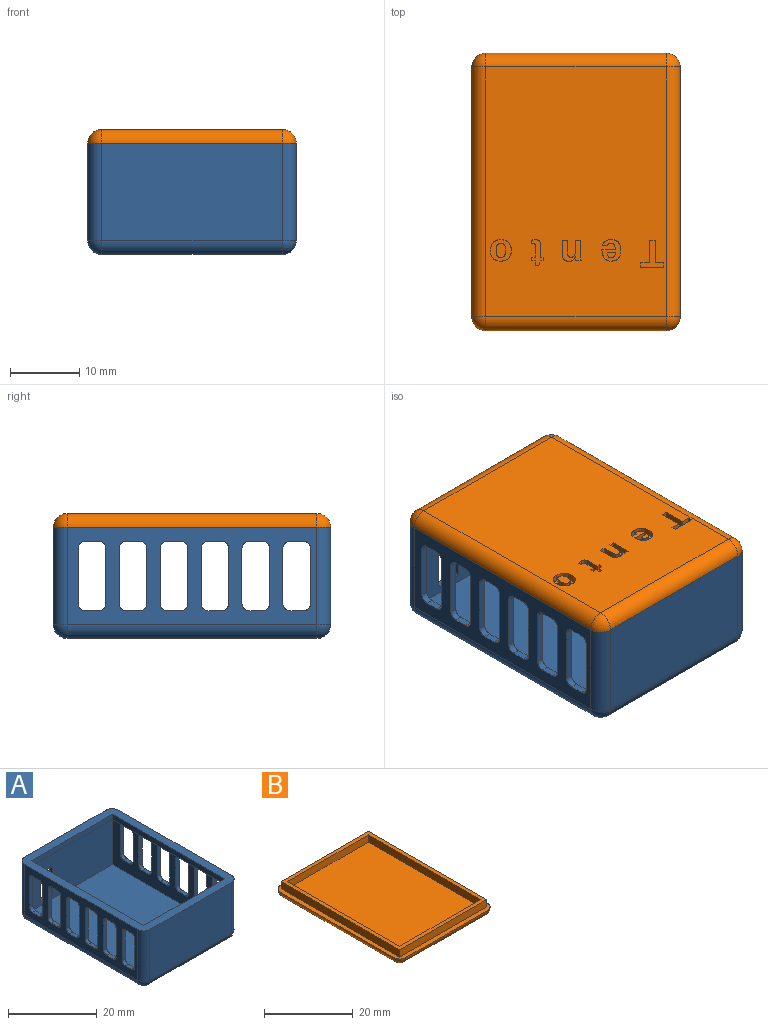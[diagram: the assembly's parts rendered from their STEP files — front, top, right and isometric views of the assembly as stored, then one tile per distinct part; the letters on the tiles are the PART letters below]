
ASSEMBLY  parts=2 mates=1
PART A: 125 faces, bbox 30x40x16 mm
  f0: plane 27.8x0.5mm, normal (0,-1,0), area 13.9mm2, adj f58,f109,f110,f116
  f1: plane 28x13mm, normal (0,-1,0), area 332.2mm2, adj f2,f4,f10,f16,f17,f18,f19,f20
  f2: plane 38x13mm, normal (-1,0,0), area 259.2mm2, adj f1,f3,f10,f42,f43,f44,f45,f46
  f3: plane 28x13mm, normal (0,1,0), area 364mm2, adj f2,f4,f10,f58
  f4: plane 38x13mm, normal (1,0,0), area 259.2mm2, adj f1,f3,f10,f24,f25,f26,f27,f28
  f5: plane 36x14mm, normal (1,0,0), area 269.2mm2, adj f9,f15,f42,f43,f44,f45,f46,f47
  f6: plane 26x14mm, normal (0,1,0), area 332.2mm2, adj f9,f14,f16,f17,f18,f20,f21,f22
  f7: plane 36x14mm, normal (-1,0,0), area 269.2mm2, adj f9,f12,f24,f25,f26,f27,f28,f29
  f8: plane 26x14mm, normal (0,-1,0), area 364mm2, adj f9,f13,f121,f123
  f9: plane 40x30mm, normal (0,0,1), area 272.9mm2, adj f5,f6,f7,f8,f112,f113,f114,f115
  f10: plane 38x28mm, normal (0,0,1), area 1064mm2, adj f1,f2,f3,f4
  f11: plane 36x26mm, normal (0,0,-1), area 936mm2, adj f12,f13,f14,f15
  f12: cylinder r=2mm len=36mm, axis (0,-1,0), area 113.1mm2, adj f7,f11,f120,f122
  f13: cylinder r=2mm len=26mm, axis (-1,0,0), area 81.7mm2, adj f8,f11,f122,f124
  f14: cylinder r=2mm len=26mm, axis (-1,0,0), area 81.7mm2, adj f6,f11,f19,f118,f120
  f15: cylinder r=2mm len=36mm, axis (0,-1,0), area 113.1mm2, adj f5,f11,f118,f124
  f16: plane 7x1mm, normal (1,0,0), area 7mm2, adj f1,f6,f20,f23
  f17: plane 3x1mm, normal (0,0,-1), area 3mm2, adj f1,f6,f20,f21
  f18: plane 7x1mm, normal (-1,0,0), area 7mm2, adj f1,f6,f21,f22
  f19: plane 3x1mm, normal (0,0,1), area 3mm2, adj f1,f14,f22,f23
  f20: cylinder r=0.5mm len=1mm, axis (0,-1,0), area 0.8mm2, adj f1,f6,f16,f17
  f21: cylinder r=0.5mm len=1mm, axis (0,-1,0), area 0.8mm2, adj f1,f6,f17,f18
  f22: cylinder r=0.5mm len=1mm, axis (0,1,0), area 0.8mm2, adj f1,f6,f18,f19
  f23: cylinder r=0.5mm len=1mm, axis (0,1,0), area 0.8mm2, adj f1,f6,f16,f19
  f24: plane 2x1mm, normal (0,0,1), area 2mm2, adj f4,f7,f105,f106
  f25: plane 8x1mm, normal (0,1,0), area 8mm2, adj f4,f7,f106,f107
  f26: plane 8x1mm, normal (0,-1,0), area 8mm2, adj f4,f7,f105,f108
  f27: plane 2x1mm, normal (0,0,1), area 2mm2, adj f4,f7,f103,f104
  f28: plane 8x1mm, normal (0,1,0), area 8mm2, adj f4,f7,f102,f103
  f29: plane 8x1mm, normal (0,-1,0), area 8mm2, adj f4,f7,f101,f104
  f30: plane 2x1mm, normal (0,0,1), area 2mm2, adj f4,f7,f97,f98
  f31: plane 8x1mm, normal (0,1,0), area 8mm2, adj f4,f7,f98,f99
  f32: plane 8x1mm, normal (0,-1,0), area 8mm2, adj f4,f7,f97,f100
  f33: plane 2x1mm, normal (0,0,1), area 2mm2, adj f4,f7,f93,f94
  f34: plane 8x1mm, normal (0,1,0), area 8mm2, adj f4,f7,f94,f95
  f35: plane 8x1mm, normal (0,-1,0), area 8mm2, adj f4,f7,f93,f96
  f36: plane 2x1mm, normal (0,0,1), area 2mm2, adj f4,f7,f89,f90
  f37: plane 8x1mm, normal (0,1,0), area 8mm2, adj f4,f7,f90,f91
  f38: plane 8x1mm, normal (0,-1,0), area 8mm2, adj f4,f7,f89,f92
  f39: plane 2x1mm, normal (0,0,1), area 2mm2, adj f4,f7,f85,f86
  f40: plane 8x1mm, normal (0,1,0), area 8mm2, adj f4,f7,f86,f87
  f41: plane 8x1mm, normal (0,-1,0), area 8mm2, adj f4,f7,f85,f88
  f42: plane 8x1mm, normal (0,-1,0), area 8mm2, adj f2,f5,f81,f83
  f43: plane 8x1mm, normal (0,1,0), area 8mm2, adj f2,f5,f82,f84
  f44: plane 2x1mm, normal (0,0,1), area 2mm2, adj f2,f5,f83,f84
  f45: plane 8x1mm, normal (0,-1,0), area 8mm2, adj f2,f5,f77,f79
  f46: plane 8x1mm, normal (0,1,0), area 8mm2, adj f2,f5,f78,f80
  f47: plane 2x1mm, normal (0,0,1), area 2mm2, adj f2,f5,f79,f80
  f48: plane 8x1mm, normal (0,-1,0), area 8mm2, adj f2,f5,f73,f75
  f49: plane 8x1mm, normal (0,1,0), area 8mm2, adj f2,f5,f74,f76
  f50: plane 2x1mm, normal (0,0,1), area 2mm2, adj f2,f5,f75,f76
  f51: plane 8x1mm, normal (0,-1,0), area 8mm2, adj f2,f5,f69,f71
  f52: plane 8x1mm, normal (0,1,0), area 8mm2, adj f2,f5,f70,f72
  f53: plane 2x1mm, normal (0,0,1), area 2mm2, adj f2,f5,f71,f72
  f54: plane 8x1mm, normal (0,-1,0), area 8mm2, adj f2,f5,f65,f67
  f55: plane 8x1mm, normal (0,1,0), area 8mm2, adj f2,f5,f66,f68
  f56: plane 2x1mm, normal (0,0,1), area 2mm2, adj f2,f5,f67,f68
  f57: plane 8x1mm, normal (0,-1,0), area 8mm2, adj f2,f5,f61,f63
  f58: plane 38x30mm, normal (0,0,-1), area 37.2mm2, adj f0,f1,f2,f3,f4,f5,f7,f61
  f59: plane 8x1mm, normal (0,1,0), area 8mm2, adj f2,f5,f62,f64
  f60: plane 2x1mm, normal (0,0,1), area 2mm2, adj f2,f5,f63,f64
  f61: cylinder r=1mm len=1mm, axis (-1,0,0), area 1.6mm2, adj f2,f5,f57,f58
  f62: cylinder r=1mm len=1mm, axis (1,0,0), area 1.6mm2, adj f2,f5,f58,f59
  f63: cylinder r=1mm len=1mm, axis (1,0,0), area 1.6mm2, adj f2,f5,f57,f60
  f64: cylinder r=1mm len=1mm, axis (-1,0,0), area 1.6mm2, adj f2,f5,f59,f60
  f65: cylinder r=1mm len=1mm, axis (-1,0,0), area 1.6mm2, adj f2,f5,f54,f58
  f66: cylinder r=1mm len=1mm, axis (1,0,0), area 1.6mm2, adj f2,f5,f55,f58
  f67: cylinder r=1mm len=1mm, axis (1,0,0), area 1.6mm2, adj f2,f5,f54,f56
  f68: cylinder r=1mm len=1mm, axis (-1,0,0), area 1.6mm2, adj f2,f5,f55,f56
  f69: cylinder r=1mm len=1mm, axis (-1,0,0), area 1.6mm2, adj f2,f5,f51,f58
  f70: cylinder r=1mm len=1mm, axis (1,0,0), area 1.6mm2, adj f2,f5,f52,f58
  f71: cylinder r=1mm len=1mm, axis (1,0,0), area 1.6mm2, adj f2,f5,f51,f53
  f72: cylinder r=1mm len=1mm, axis (-1,0,0), area 1.6mm2, adj f2,f5,f52,f53
  f73: cylinder r=1mm len=1mm, axis (-1,0,0), area 1.6mm2, adj f2,f5,f48,f58
  f74: cylinder r=1mm len=1mm, axis (1,0,0), area 1.6mm2, adj f2,f5,f49,f58
  f75: cylinder r=1mm len=1mm, axis (1,0,0), area 1.6mm2, adj f2,f5,f48,f50
  f76: cylinder r=1mm len=1mm, axis (-1,0,0), area 1.6mm2, adj f2,f5,f49,f50
  f77: cylinder r=1mm len=1mm, axis (-1,0,0), area 1.6mm2, adj f2,f5,f45,f58
  f78: cylinder r=1mm len=1mm, axis (1,0,0), area 1.6mm2, adj f2,f5,f46,f58
  f79: cylinder r=1mm len=1mm, axis (1,0,0), area 1.6mm2, adj f2,f5,f45,f47
  f80: cylinder r=1mm len=1mm, axis (-1,0,0), area 1.6mm2, adj f2,f5,f46,f47
  f81: cylinder r=1mm len=1mm, axis (-1,0,0), area 1.6mm2, adj f2,f5,f42,f58
  f82: cylinder r=1mm len=1mm, axis (1,0,0), area 1.6mm2, adj f2,f5,f43,f58
  f83: cylinder r=1mm len=1mm, axis (1,0,0), area 1.6mm2, adj f2,f5,f42,f44
  f84: cylinder r=1mm len=1mm, axis (-1,0,0), area 1.6mm2, adj f2,f5,f43,f44
  f85: cylinder r=1mm len=1mm, axis (1,0,0), area 1.6mm2, adj f4,f7,f39,f41
  f86: cylinder r=1mm len=1mm, axis (-1,0,0), area 1.6mm2, adj f4,f7,f39,f40
  f87: cylinder r=1mm len=1mm, axis (1,0,0), area 1.6mm2, adj f4,f7,f40,f58
  f88: cylinder r=1mm len=1mm, axis (-1,0,0), area 1.6mm2, adj f4,f7,f41,f58
  f89: cylinder r=1mm len=1mm, axis (1,0,0), area 1.6mm2, adj f4,f7,f36,f38
  f90: cylinder r=1mm len=1mm, axis (-1,0,0), area 1.6mm2, adj f4,f7,f36,f37
  f91: cylinder r=1mm len=1mm, axis (1,0,0), area 1.6mm2, adj f4,f7,f37,f58
  f92: cylinder r=1mm len=1mm, axis (-1,0,0), area 1.6mm2, adj f4,f7,f38,f58
  f93: cylinder r=1mm len=1mm, axis (1,0,0), area 1.6mm2, adj f4,f7,f33,f35
  f94: cylinder r=1mm len=1mm, axis (-1,0,0), area 1.6mm2, adj f4,f7,f33,f34
  f95: cylinder r=1mm len=1mm, axis (1,0,0), area 1.6mm2, adj f4,f7,f34,f58
  f96: cylinder r=1mm len=1mm, axis (-1,0,0), area 1.6mm2, adj f4,f7,f35,f58
  f97: cylinder r=1mm len=1mm, axis (1,0,0), area 1.6mm2, adj f4,f7,f30,f32
  f98: cylinder r=1mm len=1mm, axis (-1,0,0), area 1.6mm2, adj f4,f7,f30,f31
  f99: cylinder r=1mm len=1mm, axis (1,0,0), area 1.6mm2, adj f4,f7,f31,f58
  f100: cylinder r=1mm len=1mm, axis (-1,0,0), area 1.6mm2, adj f4,f7,f32,f58
  f101: cylinder r=1mm len=1mm, axis (-1,0,0), area 1.6mm2, adj f4,f7,f29,f58
  f102: cylinder r=1mm len=1mm, axis (1,0,0), area 1.6mm2, adj f4,f7,f28,f58
  f103: cylinder r=1mm len=1mm, axis (-1,0,0), area 1.6mm2, adj f4,f7,f27,f28
  f104: cylinder r=1mm len=1mm, axis (1,0,0), area 1.6mm2, adj f4,f7,f27,f29
  f105: cylinder r=1mm len=1mm, axis (1,0,0), area 1.6mm2, adj f4,f7,f24,f26
  f106: cylinder r=1mm len=1mm, axis (-1,0,0), area 1.6mm2, adj f4,f7,f24,f25
  f107: cylinder r=1mm len=1mm, axis (1,0,0), area 1.6mm2, adj f4,f7,f25,f58
  f108: cylinder r=1mm len=1mm, axis (-1,0,0), area 1.6mm2, adj f4,f7,f26,f58
  f109: plane 37.8x0.5mm, normal (1,0,0), area 18.9mm2, adj f0,f58,f111,f116
  f110: plane 37.8x0.5mm, normal (-1,0,0), area 18.9mm2, adj f0,f58,f111,f116
  f111: plane 27.8x0.5mm, normal (0,1,0), area 13.9mm2, adj f58,f109,f110,f116
  f112: plane 25.8x1.5mm, normal (0,-1,0), area 38.7mm2, adj f9,f113,f115,f116
  f113: plane 35.8x1.5mm, normal (-1,0,0), area 53.7mm2, adj f9,f112,f114,f116
  f114: plane 25.8x1.5mm, normal (0,1,0), area 38.7mm2, adj f9,f113,f115,f116
  f115: plane 35.8x1.5mm, normal (1,0,0), area 53.7mm2, adj f9,f112,f114,f116
  f116: plane 37.8x27.8mm, normal (0,0,-1), area 127.2mm2, adj f0,f109,f110,f111,f112,f113,f114,f115
  f117: cylinder r=2mm len=14mm, axis (0,0,1), area 44mm2, adj f5,f6,f9,f118
  f118: sphere r=2mm, area 6.3mm2, adj f14,f15,f117
  f119: cylinder r=2mm len=14mm, axis (0,0,-1), area 44mm2, adj f6,f7,f9,f120
  f120: sphere r=2mm, area 6.3mm2, adj f12,f14,f119
  f121: cylinder r=2mm len=14mm, axis (0,0,1), area 44mm2, adj f7,f8,f9,f122
  f122: sphere r=2mm, area 6.3mm2, adj f12,f13,f121
  f123: cylinder r=2mm len=14mm, axis (0,0,-1), area 44mm2, adj f5,f8,f9,f124
  f124: sphere r=2mm, area 6.3mm2, adj f13,f15,f123
PART B: 104 faces, bbox 30x40x4 mm
  f0: plane 36x26mm, normal (0,0,-1), area 909.2mm2, adj f13,f14,f17,f18,f25,f26,f27,f28
  f1: plane 35.8x2mm, normal (-1,0,0), area 71.6mm2, adj f2,f8,f9,f10
  f2: plane 25.8x2mm, normal (0,1,0), area 51.6mm2, adj f1,f3,f9,f10
  f3: plane 35.8x2mm, normal (1,0,0), area 71.6mm2, adj f2,f8,f9,f10
  f4: plane 37.8x2mm, normal (-1,0,0), area 75.6mm2, adj f5,f7,f9,f11
  f5: plane 27.8x2mm, normal (0,-1,0), area 55.6mm2, adj f4,f6,f9,f11
  f6: plane 37.8x2mm, normal (1,0,0), area 75.6mm2, adj f5,f7,f9,f11
  f7: plane 27.8x2mm, normal (0,1,0), area 55.6mm2, adj f4,f6,f9,f11
  f8: plane 25.8x2mm, normal (0,-1,0), area 51.6mm2, adj f1,f3,f9,f10
  f9: plane 37.8x27.8mm, normal (0,0,1), area 127.2mm2, adj f1,f2,f3,f4,f5,f6,f7,f8
  f10: plane 35.8x25.8mm, normal (0,0,1), area 923.6mm2, adj f1,f2,f3,f8
  f11: plane 40x30mm, normal (0,0,1), area 145.7mm2, adj f4,f5,f6,f7,f12,f13,f14,f15
  f12: sphere r=2mm, area 6.3mm2, adj f11,f13,f14
  f13: cylinder r=2mm len=26mm, axis (1,0,0), area 81.7mm2, adj f0,f11,f12,f15
  f14: cylinder r=2mm len=36mm, axis (0,1,0), area 113.1mm2, adj f0,f11,f12,f16
  f15: sphere r=2mm, area 6.3mm2, adj f11,f13,f17
  f16: sphere r=2mm, area 6.3mm2, adj f11,f14,f18
  f17: cylinder r=2mm len=36mm, axis (0,-1,0), area 113.1mm2, adj f0,f11,f15,f19
  f18: cylinder r=2mm len=26mm, axis (-1,0,0), area 81.7mm2, adj f0,f11,f16,f19
  f19: sphere r=2mm, area 6.3mm2, adj f11,f17,f18
  f20: extruded ~0.9x0.77mm, area 0.7mm2, adj f21,f33,f34,f102
  f21: extruded ~1.02x0.9mm, area 1.3mm2, adj f20,f22,f34,f102
  f22: extruded ~0.9x0.5mm, area 0.5mm2, adj f21,f23,f34,f102
  f23: extruded ~0.9x0.76mm, area 0.7mm2, adj f22,f24,f34,f102
  f24: extruded ~1.02x0.9mm, area 1.3mm2, adj f23,f33,f34,f102
  f25: extruded ~1.14x0.9mm, area 1.1mm2, adj f0,f26,f32,f34
  f26: extruded ~1.15x0.9mm, area 1.1mm2, adj f0,f25,f27,f34
  f27: extruded ~1.12x0.9mm, area 1.1mm2, adj f0,f26,f28,f34
  f28: extruded ~1.11x0.9mm, area 1.1mm2, adj f0,f27,f29,f34
  f29: extruded ~1.14x0.9mm, area 1.1mm2, adj f0,f28,f30,f34
  f30: extruded ~1.14x0.9mm, area 1.1mm2, adj f0,f29,f31,f34
  f31: extruded ~1.1x0.9mm, area 1.1mm2, adj f0,f30,f32,f34
  f32: extruded ~1.12x0.9mm, area 1.1mm2, adj f0,f25,f31,f34
  f33: extruded ~0.9x0.51mm, area 0.5mm2, adj f20,f24,f34,f102
  f34: plane 3.1x3.02mm, normal (0,0,-1), area 5.3mm2, adj f20,f21,f22,f23,f24,f25,f26,f27
  f35: extruded ~0.9x0.53mm, area 0.5mm2, adj f0,f36,f52,f53
  f36: extruded ~0.9x0.66mm, area 0.6mm2, adj f0,f35,f37,f53
  f37: plane 0.9x0.48mm, normal (-1,0,0), area 0.4mm2, adj f0,f36,f38,f53
  f38: extruded ~0.9x0.26mm, area 0.2mm2, adj f0,f37,f39,f53
  f39: extruded ~0.9x0.26mm, area 0.3mm2, adj f0,f38,f40,f53
  f40: extruded ~0.9x0.32mm, area 0.3mm2, adj f0,f39,f41,f53
  f41: plane 1.56x0.9mm, normal (-1,0,0), area 1.4mm2, adj f0,f40,f42,f53
  f42: plane 0.9x0.57mm, normal (0,-1,0), area 0.5mm2, adj f0,f41,f43,f53
  f43: plane 0.9x0.52mm, normal (-1,0,0), area 0.5mm2, adj f0,f42,f44,f53
  f44: plane 0.9x0.57mm, normal (0,1,0), area 0.5mm2, adj f0,f43,f45,f53
  f45: plane 0.9x0.7mm, normal (-1,0,0), area 0.6mm2, adj f0,f44,f46,f53
  f46: plane 0.9x0.49mm, normal (0,1,0), area 0.4mm2, adj f0,f45,f47,f53
  f47: plane 0.9x0.7mm, normal (0.94,0.33,0), area 0.7mm2, adj f0,f46,f48,f53
  f48: plane 0.9x0.42mm, normal (0,1,0), area 0.4mm2, adj f0,f47,f49,f53
  f49: plane 0.9x0.52mm, normal (1,0,0), area 0.5mm2, adj f0,f48,f50,f53
  f50: plane 0.9x0.38mm, normal (0,-1,0), area 0.3mm2, adj f0,f49,f51,f53
  f51: plane 1.76x0.9mm, normal (1,0,0), area 1.6mm2, adj f0,f50,f52,f53
  f52: extruded ~0.9x0.57mm, area 0.5mm2, adj f0,f35,f51,f53
  f53: plane 3.74x1.75mm, normal (0,0,-1), area 3.5mm2, adj f35,f36,f37,f38,f39,f40,f41,f42
  f54: plane 1.68x0.9mm, normal (1,0,0), area 1.5mm2, adj f0,f55,f72,f73
  f55: plane 0.9x0.77mm, normal (0,-1,0), area 0.7mm2, adj f0,f54,f56,f73
  f56: plane 1.9x0.9mm, normal (-1,0,0), area 1.7mm2, adj f0,f55,f57,f73
  f57: extruded ~0.9x0.86mm, area 0.8mm2, adj f0,f56,f58,f73
  f58: extruded ~0.9x0.73mm, area 0.7mm2, adj f0,f57,f59,f73
  f59: extruded ~0.9x0.57mm, area 0.5mm2, adj f0,f58,f60,f73
  f60: extruded ~0.9x0.5mm, area 0.6mm2, adj f0,f59,f61,f73
  f61: plane 0.9x0.01mm, normal (0,1,0), area 0mm2, adj f0,f60,f62,f73
  f62: extruded ~0.9x0.31mm, area 0.3mm2, adj f0,f61,f63,f73
  f63: extruded ~0.9x0.28mm, area 0.3mm2, adj f0,f62,f64,f73
  f64: plane 0.9x0.74mm, normal (0,1,0), area 0.7mm2, adj f0,f63,f65,f73
  f65: extruded ~0.9x0.27mm, area 0.2mm2, adj f0,f64,f66,f73
  f66: extruded ~0.9x0.39mm, area 0.4mm2, adj f0,f65,f67,f73
  f67: plane 2.32x0.9mm, normal (1,0,0), area 2.1mm2, adj f0,f66,f68,f73
  f68: plane 0.9x0.78mm, normal (0,-1,0), area 0.7mm2, adj f0,f67,f69,f73
  f69: plane 1.6x0.9mm, normal (-1,0,0), area 1.4mm2, adj f0,f68,f70,f73
  f70: extruded ~0.9x0.62mm, area 0.6mm2, adj f0,f69,f71,f73
  f71: extruded ~0.9x0.45mm, area 0.5mm2, adj f0,f70,f72,f73
  f72: extruded ~0.9x0.79mm, area 1mm2, adj f0,f54,f71,f73
  f73: plane 3.05x2.74mm, normal (0,0,-1), area 5.2mm2, adj f54,f55,f56,f57,f58,f59,f60,f61
  f74: extruded ~0.9x0.42mm, area 0.4mm2, adj f75,f91,f92,f103
  f75: extruded ~0.9x0.41mm, area 0.4mm2, adj f74,f76,f92,f103
  f76: extruded ~0.9x0.54mm, area 0.5mm2, adj f75,f77,f92,f103
  f77: plane 1.16x0.9mm, normal (0,1,0), area 1mm2, adj f76,f91,f92,f103
  f78: extruded ~1.04x0.9mm, area 1mm2, adj f0,f79,f90,f92
  f79: extruded ~1.29x0.9mm, area 1.5mm2, adj f0,f78,f80,f92
  f80: plane 0.9x0.73mm, normal (-0.09,1,0), area 0.7mm2, adj f0,f79,f81,f92
  f81: extruded ~0.9x0.52mm, area 0.6mm2, adj f0,f80,f82,f92
  f82: extruded ~0.9x0.46mm, area 0.5mm2, adj f0,f81,f83,f92
  f83: extruded ~0.9x0.66mm, area 0.6mm2, adj f0,f82,f84,f92
  f84: plane 1.92x0.9mm, normal (0,-1,0), area 1.7mm2, adj f0,f83,f85,f92
  f85: plane 0.9x0.02mm, normal (-1,0,0), area 0mm2, adj f0,f84,f86,f92
  f86: extruded ~1.25x0.9mm, area 1.2mm2, adj f0,f85,f87,f92
  f87: extruded ~0.98x0.9mm, area 1mm2, adj f0,f86,f88,f92
  f88: extruded ~1.04x0.9mm, area 1mm2, adj f0,f87,f89,f92
  f89: extruded ~1.14x0.9mm, area 1.1mm2, adj f0,f88,f90,f92
  f90: extruded ~1.17x0.9mm, area 1.1mm2, adj f0,f78,f89,f92
  f91: extruded ~0.9x0.53mm, area 0.5mm2, adj f74,f77,f92,f103
  f92: plane 3.1x2.74mm, normal (0,0,-1), area 5.1mm2, adj f74,f75,f76,f77,f78,f79,f80,f81
  f93: plane 3.27x0.9mm, normal (-1,0,0), area 2.9mm2, adj f0,f94,f100,f101
  f94: plane 1.26x0.9mm, normal (0,-1,0), area 1.1mm2, adj f0,f93,f95,f101
  f95: plane 0.9x0.63mm, normal (-1,0,0), area 0.6mm2, adj f0,f94,f96,f101
  f96: plane 3.34x0.9mm, normal (0,1,0), area 3mm2, adj f0,f95,f97,f101
  f97: plane 0.9x0.63mm, normal (1,0,0), area 0.6mm2, adj f0,f96,f98,f101
  f98: plane 1.26x0.9mm, normal (0,-1,0), area 1.1mm2, adj f0,f97,f99,f101
  f99: plane 3.27x0.9mm, normal (1,0,0), area 2.9mm2, adj f0,f98,f100,f101
  f100: plane 0.9x0.82mm, normal (0,-1,0), area 0.7mm2, adj f0,f93,f99,f101
  f101: plane 3.9x3.34mm, normal (0,0,-1), area 4.8mm2, adj f93,f94,f95,f96,f97,f98,f99,f100
  f102: plane 2.04x1.39mm, normal (0,0,-1), area 2.4mm2, adj f20,f21,f22,f23,f24,f33
  f103: plane 1.16x0.72mm, normal (0,0,-1), area 0.7mm2, adj f74,f75,f76,f77,f91
PLACE A t=(0.3,-11,-1.4)mm
PLACE B rot(axis=(0,1,0),180deg) t=(-30.7,-15.28,28.6)mm
MATE fastened B.f11 <-> A.f9  axis (0,0,-1) through (17.5,-29,13.6)mm
